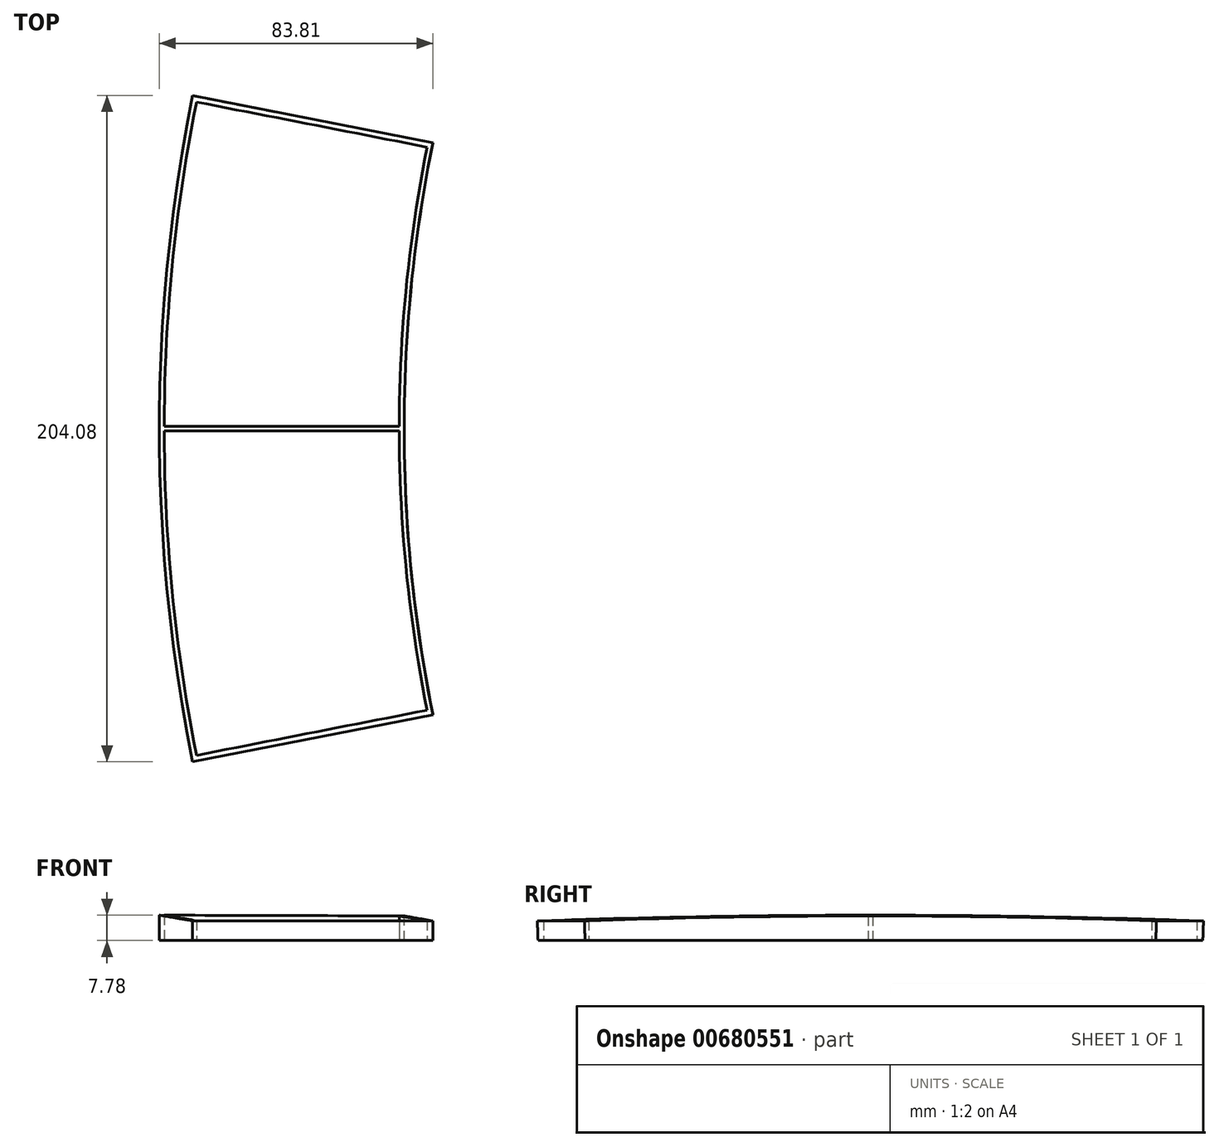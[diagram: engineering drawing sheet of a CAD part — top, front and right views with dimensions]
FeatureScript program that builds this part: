
annotation { "Feature Type Name" : "Feature", "Feature Type Description" : "" }
export const myFeature = defineFeature(function(context is Context, id is Id, definition is map)
    precondition{}
    {
        {
            var Q0;
            Q0=qCreatedBy(makeId("Front.planeOp"),FACE);
            var sketch = newSketch(context, id + "F0", { "sketchPlane" : qUnion([Q0])});
            skLineSegment(sketch, "E0", {"start": v(0, 1.91) * mm, "end": v(570.67, 0) * mm});
            skLineSegment(sketch, "E1", {"start": v(570.67, 0) * mm, "end": v(553.13, -97.53) * mm});
            skLineSegment(sketch, "E2", {"start": v(553.13, -97.53) * mm, "end": v(0, 1.91) * mm});
            skLineSegment(sketch, "E3", {"start": v(0, 1.91) * mm, "end": v(0.03, 10.91) * mm});
            skLineSegment(sketch, "E4", {"start": v(0.03, 10.91) * mm, "end": v(156.03, 10.39) * mm});
            skLineSegment(sketch, "E5", {"start": v(156.03, 10.39) * mm, "end": v(156, 1.39) * mm});
            skLineSegment(sketch, "E6", {"start": v(156, 1.39) * mm, "end": v(155.97, -7.61) * mm});
            skLineSegment(sketch, "E7", {"start": v(155.97, -7.61) * mm, "end": v(-0.03, -7.09) * mm});
            skLineSegment(sketch, "E8", {"start": v(-0.03, -7.09) * mm, "end": v(0, 1.91) * mm});
            skSolve(sketch);
        }
        {
            var Q0;
            {var subQ0=sQuery(id+"F0.wireOp",EDGE,"E3");Q0=makeQuery(id+"F0.imprint","IMPRINT",FACE,{"disambiguationData":[TD([[makeQuery(id+"F0.imprint","IMPRINT",EDGE,{"derivedFrom":subQ0}),-1.0]])]});}
            var Q1;
            {var subQ3=sQuery(id+"F0.wireOp",EDGE,"E6");Q1=makeQuery(id+"F0.imprint","IMPRINT",FACE,{"disambiguationData":[TD([[makeQuery(id+"F0.imprint","IMPRINT",EDGE,{"derivedFrom":subQ3}),-1.0]])]});}
            var Q2;
            {var subQ0=sQuery(id+"F0.wireOp",EDGE,"E8");Q2=makeQuery(id+"F0.imprint","IMPRINT",FACE,{"disambiguationData":[TD([[makeQuery(id+"F0.imprint","IMPRINT",EDGE,{"derivedFrom":subQ0}),-1.0]])]});}
            var Q3;
            Q3=sQuery(id+"F0.wireOp",EDGE,"E1");
            revolve(context, id + "F1", {"entities" : qUnion([Q0, Q1, Q2]), "axis" : qUnion([Q3]), "revolveType" : RevolveType.SYMMETRIC, "angle" : 22.5 * degree});
        }
        {
            var Q0;
            Q0=qCreatedBy(makeId("Front.planeOp"),FACE);
            var sketch = newSketch(context, id + "F2", { "sketchPlane" : qUnion([Q0])});
            skLineSegment(sketch, "E9.bottom", {"start": v(-6.73, 29.38) * mm, "end": v(170.86, 29.38) * mm});
            skLineSegment(sketch, "E9.top", {"start": v(-6.73, 7) * mm, "end": v(170.86, 7) * mm});
            skLineSegment(sketch, "E9.left", {"start": v(-6.73, 29.38) * mm, "end": v(-6.73, 7) * mm});
            skLineSegment(sketch, "E9.right", {"start": v(170.86, 29.38) * mm, "end": v(170.86, 7) * mm});
            skLineSegment(sketch, "E10.bottom", {"start": v(-6.11, 1) * mm, "end": v(170.86, 1) * mm});
            skLineSegment(sketch, "E10.top", {"start": v(-6.11, -14.01) * mm, "end": v(170.86, -14.01) * mm});
            skLineSegment(sketch, "E10.left", {"start": v(-6.11, 1) * mm, "end": v(-6.11, -14.01) * mm});
            skLineSegment(sketch, "E10.right", {"start": v(170.86, 1) * mm, "end": v(170.86, -14.01) * mm});
            skLineSegment(sketch, "E11", {"start": v(39, 29.38) * mm, "end": v(39, 7) * mm});
            skLineSegment(sketch, "E12", {"start": v(117, 29.38) * mm, "end": v(117, 7) * mm});
            skLineSegment(sketch, "E13", {"start": v(584.9, 30.18) * mm, "end": v(584.9, -42.22) * mm});
            skSolve(sketch);
        }
        {
            var Q0;
            {var subQ0=sQuery(id+"F2.wireOp",EDGE,"E9.left");Q0=makeQuery(id+"F2.imprint","IMPRINT",FACE,{"disambiguationData":[TD([[makeQuery(id+"F2.imprint","IMPRINT",EDGE,{"derivedFrom":subQ0}),1.0]])]});}
            var Q1;
            Q1=makeQuery(id+"F2.imprint","IMPRINT",FACE,{"disambiguationData":[TD([[makeQuery(id+"F2.imprint","IMPRINT",EDGE,{"derivedFrom":sQuery(id+"F2.wireOp",EDGE,"E10.bottom")}),-1.0]])]});
            var Q2;
            {var subQ0=sQuery(id+"F2.wireOp",EDGE,"E9.right");Q2=makeQuery(id+"F2.imprint","IMPRINT",FACE,{"disambiguationData":[TD([[makeQuery(id+"F2.imprint","IMPRINT",EDGE,{"derivedFrom":subQ0}),-1.0]])]});}
            var Q3;
            Q3=sQuery(id+"F2.wireOp",EDGE,"E13");
            revolve(context, id + "F3", {"operationType" : NewBodyOperationType.REMOVE, "entities" : qUnion([Q0, Q1, Q2]), "axis" : qUnion([Q3]), "revolveType" : RevolveType.FULL});
        }
        {
            var Q0;
            Q0=qCreatedBy(makeId("Front.planeOp"),FACE);
            var sketch = newSketch(context, id + "F4", { "sketchPlane" : qUnion([Q0])});
            skLineSegment(sketch, "E14", {"start": v(0, 1.91) * mm, "end": v(499.78, -162.1) * mm});
            skLineSegment(sketch, "E15", {"start": v(499.78, -162.1) * mm, "end": v(528.06, -75.91) * mm});
            skLineSegment(sketch, "E16.bottom", {"start": v(-10.85, 12.62) * mm, "end": v(40.5, 12.62) * mm});
            skLineSegment(sketch, "E16.top", {"start": v(-10.85, -3.91) * mm, "end": v(40.5, -3.91) * mm});
            skLineSegment(sketch, "E16.left", {"start": v(-10.85, 12.62) * mm, "end": v(-10.85, -3.91) * mm});
            skLineSegment(sketch, "E16.right", {"start": v(40.5, 12.62) * mm, "end": v(40.5, -3.91) * mm});
            skLineSegment(sketch, "E17.bottom", {"start": v(115.5, 16.15) * mm, "end": v(167.08, 16.15) * mm});
            skLineSegment(sketch, "E17.top", {"start": v(115.5, -3.91) * mm, "end": v(167.08, -3.91) * mm});
            skLineSegment(sketch, "E17.left", {"start": v(115.5, 16.15) * mm, "end": v(115.5, -3.91) * mm});
            skLineSegment(sketch, "E17.right", {"start": v(167.08, 16.15) * mm, "end": v(167.08, -3.91) * mm});
            skSolve(sketch);
        }
        {
            var Q0;
            Q0=makeQuery(id+"F4.imprint","IMPRINT",FACE,{"disambiguationData":[TD([[makeQuery(id+"F4.imprint","IMPRINT",EDGE,{"derivedFrom":sQuery(id+"F4.wireOp",EDGE,"E16.bottom")}),-1.0]])]});
            var Q1;
            Q1=makeQuery(id+"F4.imprint","IMPRINT",FACE,{"disambiguationData":[TD([[makeQuery(id+"F4.imprint","IMPRINT",EDGE,{"derivedFrom":sQuery(id+"F4.wireOp",EDGE,"E17.bottom")}),-1.0]])]});
            var Q2;
            Q2=sQuery(id+"F4.wireOp",EDGE,"E15");
            revolve(context, id + "F5", {"operationType" : NewBodyOperationType.REMOVE, "entities" : qUnion([Q0, Q1]), "axis" : qUnion([Q2]), "revolveType" : RevolveType.SYMMETRIC, "angle" : 30 * degree});
        }
        {
            var Q0;
            Q0=qCreatedBy(makeId("Front.planeOp"),FACE);
            var sketch = newSketch(context, id + "F6", { "sketchPlane" : qUnion([Q0])});
            skLineSegment(sketch, "E18", {"start": v(0, 1.91) * mm, "end": v(570.67, 0) * mm});
            skLineSegment(sketch, "E19", {"start": v(570.67, 0) * mm, "end": v(553.13, -97.53) * mm});
            skLineSegment(sketch, "E20", {"start": v(553.13, -97.53) * mm, "end": v(0, 1.91) * mm});
            skLineSegment(sketch, "E21", {"start": v(0, 1.91) * mm, "end": v(0.02, 8.91) * mm});
            skLineSegment(sketch, "E22", {"start": v(0.02, 8.91) * mm, "end": v(156.02, 8.39) * mm});
            skLineSegment(sketch, "E23", {"start": v(156.02, 8.39) * mm, "end": v(156, 1.39) * mm});
            skLineSegment(sketch, "E24", {"start": v(156, 1.39) * mm, "end": v(155.97, -7.61) * mm});
            skLineSegment(sketch, "E25", {"start": v(155.97, -7.61) * mm, "end": v(-0.03, -7.09) * mm});
            skLineSegment(sketch, "E26", {"start": v(-0.03, -7.09) * mm, "end": v(0, 1.91) * mm});
            skLineSegment(sketch, "E27", {"start": v(0.02, 8.91) * mm, "end": v(16.4, 17.17) * mm});
            skLineSegment(sketch, "E28", {"start": v(16.4, 17.17) * mm, "end": v(144.17, 14.47) * mm});
            skLineSegment(sketch, "E29", {"start": v(144.17, 14.47) * mm, "end": v(156.02, 8.39) * mm});
            skSolve(sketch);
        }
        {
            var Q0;
            Q0=makeQuery(id+"F6.imprint","IMPRINT",FACE,{"disambiguationData":[TD([[makeQuery(id+"F6.imprint","IMPRINT",EDGE,{"derivedFrom":sQuery(id+"F6.wireOp",EDGE,"E22")}),1.0]])]});
            var Q1;
            Q1=sQuery(id+"F6.wireOp",EDGE,"E19");
            revolve(context, id + "F7", {"operationType" : NewBodyOperationType.REMOVE, "entities" : qUnion([Q0]), "axis" : qUnion([Q1]), "revolveType" : RevolveType.SYMMETRIC, "angle" : 30 * degree});
        }
        {
            var Q0;
            Q0=makeQuery(id+"F3.boolean.opBoolean","COPY",FACE,{"derivedFrom":makeQuery(id+"F3.opRevolve","SWEPT_FACE",FACE,{"disambiguationData":[OSD([sQuery(id+"F2.wireOp",EDGE,"E10.bottom")])]})});
            var sketch = newSketch(context, id + "F8", { "sketchPlane" : qUnion([Q0])});
            skLineSegment(sketch, "E30", {"start": v(51.89, 100.07) * mm, "end": v(122.55, 86.24) * mm});
            skLineSegment(sketch, "E31", {"start": v(51.89, 100.07) * mm, "end": v(52.17, 101.54) * mm});
            skLineSegment(sketch, "E32", {"start": v(122.55, 86.24) * mm, "end": v(122.84, 87.7) * mm});
            skLineSegment(sketch, "E33", {"start": v(52.17, -101.54) * mm, "end": v(51.89, -100.07) * mm});
            skLineSegment(sketch, "E34", {"start": v(51.89, -100.07) * mm, "end": v(122.55, -86.24) * mm});
            skLineSegment(sketch, "E35", {"start": v(122.84, -87.7) * mm, "end": v(122.55, -86.24) * mm});
            skLineSegment(sketch, "E36", {"start": v(40.5, -0.04) * mm, "end": v(42, -0.04) * mm});
            skLineSegment(sketch, "E37", {"start": v(115.5, 0) * mm, "end": v(114, 0) * mm});
            skArc(sketch, "E38", {"start": v(122.55, 86.24) * mm, "mid": v(114, 0) * mm, "end": v(122.55, -86.24) * mm});
            skArc(sketch, "E39", {"start": v(51.89, 100.07) * mm, "mid": v(42, 0) * mm, "end": v(51.89, -100.07) * mm});
            skLineSegment(sketch, "E40", {"start": v(42, -0.75) * mm, "end": v(114, -0.75) * mm});
            skLineSegment(sketch, "E41", {"start": v(114, 0.75) * mm, "end": v(42, 0.75) * mm});
            skSolve(sketch);
        }
        {
            var Q0;
            {var subQ1=sQuery(id+"F8.wireOp",EDGE,"E30");Q0=makeQuery(id+"F8.imprint","IMPRINT",FACE,{"disambiguationData":[TD([[makeQuery(id+"F8.imprint","IMPRINT",EDGE,{"derivedFrom":subQ1}),-1.0]])]});}
            var Q1;
            {var subQ0=sQuery(id+"F8.wireOp",EDGE,"E34");Q1=makeQuery(id+"F8.imprint","IMPRINT",FACE,{"disambiguationData":[TD([[makeQuery(id+"F8.imprint","IMPRINT",EDGE,{"derivedFrom":subQ0}),1.0]])]});}
            extrude(context, id + "F9", {"entities" : qUnion([Q0, Q1]), "operationType" : NewBodyOperationType.REMOVE, "oppositeDirection" : true, "depth" : 25 * mm, "offsetDistance" : 25 * mm});
        }
    });
